# Revit family: ER
name_source: partatom
category: Wyposażenie mechaniczne
revit_build: Autodesk Revit 2017 (Build: 20160225_1515(x64)
units: mm (PartAtom-declared; Revit-internal decimal feet)

## family parameters
Oparty na płaszczyźnie roboczej = Nie
Punkt obliczania pomieszczeń = Nie
Tnij formami wycięć po wczytaniu = Nie
Typ części = Normalny
Współdzielony = Nie
Wymiar okrągłego złącza = Użyj średnicy
Zawsze pionowo = Tak

## types (28) — shared parameters
Date = 01.2019
Electrical_motor_diameter = 30 mm  [stored 0.0984252 ft]
Electrical_motor_length_front = 5 mm  [stored 0.0164042 ft]
Frequency = 50 Hz
Producent = Rosenberg
URL = https://www.rosenberg.pl
Version = 1
Voltage = 230 V

## per-type parameters (varying)
- 400-4.4EC: 250_cover=Nie; 315_cover=Nie; 400_cover=Tak; 450_cover=Nie; 560_cover=Nie; 630_cover=Nie; Air_flow=3245.0 m³/h; Current=1 A; Electrical_motor_length_back=60 mm  [stored 0.19685 ft]; Inner_diameter=403 mm; Length=155 mm  [stored 0.50853 ft]; Model=400-4.4EC; Outer_diameter=466 mm; Power=0 kW; Pressure=67.0 Pa; Propeller_length=197 mm  [stored 0.646325 ft]; Protection_class=IP54; Radius_inner=202 mm; Radius_outer=233 mm; Sheet_metal_thickness=6 mm  [stored 0.019685 ft]; Thickness=88 mm  [stored 0.288714 ft]; Weight=7.50 kg; Wymiar_obudowy/2=270 mm; diameter=409 mm; max.Ambient_temperature=60 °C
- 315-2: 250_cover=Nie; 315_cover=Tak; 400_cover=Nie; 450_cover=Nie; 560_cover=Nie; 630_cover=Nie; Air_flow=2796.0 m³/h; Current=3 A; Electrical_motor_length_back=85 mm  [stored 0.278871 ft]; Inner_diameter=317 mm; Length=130 mm  [stored 0.426509 ft]; Model=315-2; Outer_diameter=382 mm; Power=1 kW; Pressure=20.0 Pa; Propeller_length=154 mm; Protection_class=IP54; Radius_inner=159 mm; Radius_outer=191 mm  [stored 0.62664 ft]; Sheet_metal_thickness=6 mm  [stored 0.019685 ft]; Thickness=49 mm  [stored 0.160761 ft]; Weight=10.40 kg; Wymiar_obudowy/2=185 mm  [stored 0.606955 ft]; diameter=323 mm; max.Ambient_temperature=50 °C
- 250-2.3CF: 250_cover=Tak; 315_cover=Nie; 400_cover=Nie; 450_cover=Nie; 560_cover=Nie; 630_cover=Nie; Air_flow=0.0 m³/h; Current=1 A; Electrical_motor_length_back=61 mm  [stored 0.200131 ft]; Inner_diameter=254 mm; Length=95 mm  [stored 0.31168 ft]; Model=250-2.3CF; Outer_diameter=306 mm; Power=0 kW; Pressure=0.0 Pa; Propeller_length=122 mm; Protection_class=IP44; Radius_inner=127 mm  [stored 0.416667 ft]; Radius_outer=153 mm  [stored 0.501969 ft]; Sheet_metal_thickness=6 mm  [stored 0.019685 ft]; Thickness=46 mm  [stored 0.150919 ft]; Weight=3.50 kg; Wymiar_obudowy/2=156 mm  [stored 0.511811 ft]; diameter=260 mm; max.Ambient_temperature=60 °C
- 350-2: 250_cover=Nie; 315_cover=Nie; 400_cover=Tak; 450_cover=Nie; 560_cover=Nie; 630_cover=Nie; Air_flow=3738.0 m³/h; Current=4 A; Electrical_motor_length_back=60 mm  [stored 0.19685 ft]; Inner_diameter=358 mm; Length=135 mm  [stored 0.442913 ft]; Model=350-2; Outer_diameter=421 mm; Power=1 kW; Pressure=217.0 Pa; Propeller_length=174 mm  [stored 0.570866 ft]; Protection_class=IP54; Radius_inner=179 mm  [stored 0.58727 ft]; Radius_outer=211 mm; Sheet_metal_thickness=12 mm  [stored 0.0393701 ft]; Thickness=74 mm  [stored 0.242782 ft]; Weight=12.50 kg; Wymiar_obudowy/2=243 mm; diameter=364 mm; max.Ambient_temperature=40 °C
- 500-6: 250_cover=Nie; 315_cover=Nie; 400_cover=Nie; 450_cover=Tak; 560_cover=Nie; 630_cover=Nie; Air_flow=3652.0 m³/h; Current=1 A; Electrical_motor_length_back=60 mm  [stored 0.19685 ft]; Inner_diameter=504 mm; Length=165 mm; Model=500-6; Outer_diameter=567 mm; Power=0 kW; Pressure=49.0 Pa; Propeller_length=247 mm; Protection_class=IP54; Radius_inner=252 mm; Radius_outer=284 mm; Sheet_metal_thickness=12 mm  [stored 0.0393701 ft]; Thickness=88 mm  [stored 0.288714 ft]; Weight=10.50 kg; Wymiar_obudowy/2=270 mm; diameter=510 mm; max.Ambient_temperature=60 °C
- 560-4: 250_cover=Nie; 315_cover=Nie; 400_cover=Nie; 450_cover=Nie; 560_cover=Tak; 630_cover=Nie; Air_flow=7173.0 m³/h; Current=4 A; Electrical_motor_length_back=60 mm  [stored 0.19685 ft]; Inner_diameter=561 mm; Length=210 mm  [stored 0.688976 ft]; Model=560-4; Outer_diameter=630 mm; Power=1 kW; Pressure=124.0 Pa; Propeller_length=275 mm; Protection_class=IP54; Radius_inner=280 mm; Radius_outer=315 mm; Sheet_metal_thickness=12 mm  [stored 0.0393701 ft]; Thickness=88 mm  [stored 0.288714 ft]; Weight=16.50 kg; Wymiar_obudowy/2=270 mm; diameter=567 mm; max.Ambient_temperature=40 °C
- 630-4: 250_cover=Nie; 315_cover=Nie; 400_cover=Nie; 450_cover=Nie; 560_cover=Nie; 630_cover=Tak; Air_flow=12288.0 m³/h; Current=10 A; Electrical_motor_length_back=60 mm  [stored 0.19685 ft]; Inner_diameter=635 mm; Length=220 mm  [stored 0.721785 ft]; Model=630-4; Outer_diameter=704 mm; Power=2 kW; Pressure=204.0 Pa; Propeller_length=313 mm; Protection_class=IP54; Radius_inner=318 mm; Radius_outer=352 mm; Sheet_metal_thickness=12 mm  [stored 0.0393701 ft]; Thickness=88 mm  [stored 0.288714 ft]; Weight=22.50 kg; Wymiar_obudowy/2=270 mm; diameter=641 mm; max.Ambient_temperature=40 °C
- 315-2.4FF: 250_cover=Nie; 315_cover=Tak; 400_cover=Nie; 450_cover=Nie; 560_cover=Nie; 630_cover=Nie; Air_flow=2499.0 m³/h; Current=2 A; Electrical_motor_length_back=85 mm  [stored 0.278871 ft]; Inner_diameter=317 mm; Length=130 mm  [stored 0.426509 ft]; Model=315-2.4FF; Outer_diameter=382 mm; Power=0 kW; Pressure=168.0 Pa; Propeller_length=154 mm; Protection_class=IP54; Radius_inner=159 mm; Radius_outer=191 mm  [stored 0.62664 ft]; Sheet_metal_thickness=6 mm  [stored 0.019685 ft]; Thickness=49 mm  [stored 0.160761 ft]; Weight=6.20 kg; Wymiar_obudowy/2=185 mm  [stored 0.606955 ft]; diameter=323 mm; max.Ambient_temperature=50 °C
- 315-4.4DA: 250_cover=Nie; 315_cover=Tak; 400_cover=Nie; 450_cover=Nie; 560_cover=Nie; 630_cover=Nie; Air_flow=0.0 m³/h; Current=1 A; Electrical_motor_length_back=85 mm  [stored 0.278871 ft]; Inner_diameter=317 mm; Length=130 mm  [stored 0.426509 ft]; Model=315-4.4DA; Outer_diameter=382 mm; Power=0 kW; Pressure=0.0 Pa; Propeller_length=154 mm; Protection_class=IP54; Radius_inner=159 mm; Radius_outer=191 mm  [stored 0.62664 ft]; Sheet_metal_thickness=6 mm  [stored 0.019685 ft]; Thickness=49 mm  [stored 0.160761 ft]; Weight=6.00 kg; Wymiar_obudowy/2=185 mm  [stored 0.606955 ft]; diameter=323 mm; max.Ambient_temperature=65 °C
- 350-4: 250_cover=Nie; 315_cover=Nie; 400_cover=Tak; 450_cover=Nie; 560_cover=Nie; 630_cover=Nie; Air_flow=2255.0 m³/h; Current=1 A; Electrical_motor_length_back=60 mm  [stored 0.19685 ft]; Inner_diameter=358 mm; Length=135 mm  [stored 0.442913 ft]; Model=350-4; Outer_diameter=421 mm; Power=0 kW; Pressure=57.0 Pa; Propeller_length=174 mm  [stored 0.570866 ft]; Protection_class=IP54; Radius_inner=179 mm  [stored 0.58727 ft]; Radius_outer=211 mm; Sheet_metal_thickness=12 mm  [stored 0.0393701 ft]; Thickness=74 mm  [stored 0.242782 ft]; Weight=10.00 kg; Wymiar_obudowy/2=243 mm; diameter=364 mm; max.Ambient_temperature=65 °C
- 350-4.4EC: 250_cover=Nie; 315_cover=Nie; 400_cover=Tak; 450_cover=Nie; 560_cover=Nie; 630_cover=Nie; Air_flow=2150.0 m³/h; Current=1 A; Electrical_motor_length_back=60 mm  [stored 0.19685 ft]; Inner_diameter=358 mm; Length=135 mm  [stored 0.442913 ft]; Model=350-4.4EC; Outer_diameter=421 mm; Power=0 kW; Pressure=78.0 Pa; Propeller_length=174 mm  [stored 0.570866 ft]; Protection_class=IP54; Radius_inner=179 mm  [stored 0.58727 ft]; Radius_outer=211 mm; Sheet_metal_thickness=12 mm  [stored 0.0393701 ft]; Thickness=74 mm  [stored 0.242782 ft]; Weight=7.00 kg; Wymiar_obudowy/2=243 mm; diameter=364 mm; max.Ambient_temperature=70 °C
- 400-6.4DA: 250_cover=Nie; 315_cover=Nie; 400_cover=Tak; 450_cover=Nie; 560_cover=Nie; 630_cover=Nie; Air_flow=0.0 m³/h; Current=0 A; Electrical_motor_length_back=60 mm  [stored 0.19685 ft]; Inner_diameter=403 mm; Length=155 mm  [stored 0.50853 ft]; Model=400-6.DA; Outer_diameter=466 mm; Power=0 kW; Pressure=0.0 Pa; Propeller_length=197 mm  [stored 0.646325 ft]; Protection_class=IP54; Radius_inner=202 mm; Radius_outer=233 mm; Sheet_metal_thickness=6 mm  [stored 0.019685 ft]; Thickness=88 mm  [stored 0.288714 ft]; Weight=8.50 kg; Wymiar_obudowy/2=270 mm; diameter=409 mm; max.Ambient_temperature=55 °C
- 450-4.5DF: 250_cover=Nie; 315_cover=Nie; 400_cover=Nie; 450_cover=Tak; 560_cover=Nie; 630_cover=Nie; Air_flow=4055.0 m³/h; Current=1 A; Electrical_motor_length_back=60 mm  [stored 0.19685 ft]; Inner_diameter=452 mm; Length=160 mm  [stored 0.524934 ft]; Model=450-4.5DF; Outer_diameter=515 mm; Power=0 kW; Pressure=92.0 Pa; Propeller_length=221 mm; Protection_class=IP54; Radius_inner=226 mm  [stored 0.74147 ft]; Radius_outer=258 mm; Sheet_metal_thickness=6 mm  [stored 0.019685 ft]; Thickness=88 mm  [stored 0.288714 ft]; Weight=10.00 kg; Wymiar_obudowy/2=270 mm; diameter=458 mm; max.Ambient_temperature=5 °C
- 450-6.5DF: 250_cover=Nie; 315_cover=Nie; 400_cover=Nie; 450_cover=Tak; 560_cover=Nie; 630_cover=Nie; Air_flow=0.0 m³/h; Current=1 A; Electrical_motor_length_back=60 mm  [stored 0.19685 ft]; Inner_diameter=452 mm; Length=160 mm  [stored 0.524934 ft]; Model=450-6.5DF; Outer_diameter=515 mm; Power=0 kW; Pressure=0.0 Pa; Propeller_length=221 mm; Protection_class=IP54; Radius_inner=226 mm  [stored 0.74147 ft]; Radius_outer=258 mm; Sheet_metal_thickness=6 mm  [stored 0.019685 ft]; Thickness=88 mm  [stored 0.288714 ft]; Weight=9.00 kg; Wymiar_obudowy/2=270 mm; diameter=458 mm; max.Ambient_temperature=70 °C
- 500-4.5FA: 250_cover=Nie; 315_cover=Nie; 400_cover=Nie; 450_cover=Tak; 560_cover=Nie; 630_cover=Nie; Air_flow=5483.0 m³/h; Current=2 A; Electrical_motor_length_back=60 mm  [stored 0.19685 ft]; Inner_diameter=504 mm; Length=165 mm; Model=500-4.5FA; Outer_diameter=567 mm; Power=0 kW; Pressure=108.0 Pa; Propeller_length=247 mm; Protection_class=IP54; Radius_inner=252 mm; Radius_outer=284 mm; Sheet_metal_thickness=12 mm  [stored 0.0393701 ft]; Thickness=88 mm  [stored 0.288714 ft]; Weight=12.00 kg; Wymiar_obudowy/2=270 mm; diameter=510 mm; max.Ambient_temperature=50 °C
- 560-6.5FA: 250_cover=Nie; 315_cover=Nie; 400_cover=Nie; 450_cover=Nie; 560_cover=Tak; 630_cover=Nie; Air_flow=5680.0 m³/h; Current=2 A; Electrical_motor_length_back=60 mm  [stored 0.19685 ft]; Inner_diameter=561 mm; Length=210 mm  [stored 0.688976 ft]; Model=560-6.5FA; Outer_diameter=630 mm; Power=0 kW; Pressure=65.0 Pa; Propeller_length=275 mm; Protection_class=IP54; Radius_inner=280 mm; Radius_outer=315 mm; Sheet_metal_thickness=12 mm  [stored 0.0393701 ft]; Thickness=88 mm  [stored 0.288714 ft]; Weight=14.00 kg; Wymiar_obudowy/2=270 mm; diameter=567 mm; max.Ambient_temperature=60 °C
- 630-6.5HA: 250_cover=Nie; 315_cover=Nie; 400_cover=Nie; 450_cover=Nie; 560_cover=Nie; 630_cover=Tak; Air_flow=7647.0 m³/h; Current=2 A; Electrical_motor_length_back=60 mm  [stored 0.19685 ft]; Inner_diameter=635 mm; Length=220 mm  [stored 0.721785 ft]; Model=630-6.5HA; Outer_diameter=704 mm; Power=0 kW; Pressure=70.0 Pa; Propeller_length=313 mm; Protection_class=IP54; Radius_inner=318 mm; Radius_outer=352 mm; Sheet_metal_thickness=12 mm  [stored 0.0393701 ft]; Thickness=88 mm  [stored 0.288714 ft]; Weight=22.50 kg; Wymiar_obudowy/2=270 mm; diameter=641 mm; max.Ambient_temperature=60 °C
- 710-6: 250_cover=Nie; 315_cover=Nie; 400_cover=Nie; 450_cover=Nie; 560_cover=Nie; 630_cover=Nie; Air_flow=10559.0 m³/h; Current=5 A; Electrical_motor_length_back=60 mm  [stored 0.19685 ft]; Inner_diameter=711 mm; Length=230 mm  [stored 0.754593 ft]; Model=710-6; Outer_diameter=785 mm; Power=1 kW; Pressure=91.0 Pa; Propeller_length=351 mm; Protection_class=IP54; Radius_inner=356 mm; Radius_outer=393 mm; Sheet_metal_thickness=12 mm  [stored 0.0393701 ft]; Thickness=88 mm  [stored 0.288714 ft]; Weight=31.00 kg; Wymiar_obudowy/2=270 mm; diameter=717 mm; max.Ambient_temperature=70 °C
- 200-2.3BF: 250_cover=Tak; 315_cover=Nie; 400_cover=Nie; 450_cover=Nie; 560_cover=Nie; 630_cover=Nie; Air_flow=0.0 m³/h; Current=0 A; Electrical_motor_length_back=61 mm  [stored 0.200131 ft]; Inner_diameter=204 mm; Length=93 mm  [stored 0.305118 ft]; Model=200-2.3BF; Outer_diameter=255 mm; Power=0 kW; Pressure=0.0 Pa; Propeller_length=97 mm; Protection_class=IP44; Radius_inner=102 mm; Radius_outer=128 mm; Sheet_metal_thickness=6 mm  [stored 0.019685 ft]; Thickness=46 mm  [stored 0.150919 ft]; Weight=2.50 kg; Wymiar_obudowy/2=156 mm  [stored 0.511811 ft]; diameter=210 mm  [stored 0.688976 ft]; max.Ambient_temperature=70 °C
- 200-4.3BF: 250_cover=Tak; 315_cover=Nie; 400_cover=Nie; 450_cover=Nie; 560_cover=Nie; 630_cover=Nie; Air_flow=0.0 m³/h; Current=0 A; Electrical_motor_length_back=61 mm  [stored 0.200131 ft]; Inner_diameter=204 mm; Length=93 mm  [stored 0.305118 ft]; Model=200-4.3BF; Outer_diameter=255 mm; Power=0 kW; Pressure=0.0 Pa; Propeller_length=97 mm; Protection_class=IP44; Radius_inner=102 mm; Radius_outer=128 mm; Sheet_metal_thickness=6 mm  [stored 0.019685 ft]; Thickness=46 mm  [stored 0.150919 ft]; Weight=2.50 kg; Wymiar_obudowy/2=156 mm  [stored 0.511811 ft]; diameter=210 mm  [stored 0.688976 ft]; max.Ambient_temperature=70 °C
- 250-4.3CF: 250_cover=Tak; 315_cover=Nie; 400_cover=Nie; 450_cover=Nie; 560_cover=Nie; 630_cover=Nie; Air_flow=0.0 m³/h; Current=0 A; Electrical_motor_length_back=61 mm  [stored 0.200131 ft]; Inner_diameter=254 mm; Length=95 mm  [stored 0.31168 ft]; Model=250-4.3CF; Outer_diameter=306 mm; Power=0 kW; Pressure=0.0 Pa; Propeller_length=122 mm; Protection_class=IP44; Radius_inner=127 mm  [stored 0.416667 ft]; Radius_outer=153 mm  [stored 0.501969 ft]; Sheet_metal_thickness=6 mm  [stored 0.019685 ft]; Thickness=46 mm  [stored 0.150919 ft]; Weight=3.50 kg; Wymiar_obudowy/2=156 mm  [stored 0.511811 ft]; diameter=260 mm; max.Ambient_temperature=70 °C
- 300-2.3EF: 250_cover=Nie; 315_cover=Tak; 400_cover=Nie; 450_cover=Nie; 560_cover=Nie; 630_cover=Nie; Air_flow=1848.0 m³/h; Current=1 A; Electrical_motor_length_back=85 mm  [stored 0.278871 ft]; Inner_diameter=317 mm; Length=130 mm  [stored 0.426509 ft]; Model=300-2.3EF; Outer_diameter=382 mm; Power=0 kW; Pressure=126.0 Pa; Propeller_length=154 mm; Protection_class=IP44; Radius_inner=159 mm; Radius_outer=191 mm  [stored 0.62664 ft]; Sheet_metal_thickness=6 mm  [stored 0.019685 ft]; Thickness=49 mm  [stored 0.160761 ft]; Weight=5.50 kg; Wymiar_obudowy/2=185 mm  [stored 0.606955 ft]; diameter=323 mm; max.Ambient_temperature=55 °C
- 300-4.3DF: 250_cover=Nie; 315_cover=Tak; 400_cover=Nie; 450_cover=Nie; 560_cover=Nie; 630_cover=Nie; Air_flow=0.0 m³/h; Current=0 A; Electrical_motor_length_back=85 mm  [stored 0.278871 ft]; Inner_diameter=317 mm; Length=130 mm  [stored 0.426509 ft]; Model=300-4.3DF; Outer_diameter=382 mm; Power=0 kW; Pressure=0.0 Pa; Propeller_length=154 mm; Protection_class=IP44; Radius_inner=159 mm; Radius_outer=191 mm  [stored 0.62664 ft]; Sheet_metal_thickness=6 mm  [stored 0.019685 ft]; Thickness=49 mm  [stored 0.160761 ft]; Weight=5.50 kg; Wymiar_obudowy/2=185 mm  [stored 0.606955 ft]; diameter=323 mm; max.Ambient_temperature=55 °C
- 315-6.4DA: 250_cover=Nie; 315_cover=Tak; 400_cover=Nie; 450_cover=Nie; 560_cover=Nie; 630_cover=Nie; Air_flow=0.0 m³/h; Current=0 A; Electrical_motor_length_back=85 mm  [stored 0.278871 ft]; Inner_diameter=317 mm; Length=130 mm  [stored 0.426509 ft]; Model=315-6.4DA; Outer_diameter=382 mm; Power=0 kW; Pressure=0.0 Pa; Propeller_length=154 mm; Protection_class=IP54; Radius_inner=159 mm; Radius_outer=191 mm  [stored 0.62664 ft]; Sheet_metal_thickness=6 mm  [stored 0.019685 ft]; Thickness=49 mm  [stored 0.160761 ft]; Weight=6.50 kg; Wymiar_obudowy/2=185 mm  [stored 0.606955 ft]; diameter=323 mm; max.Ambient_temperature=60 °C
- 350-6.4DA: 250_cover=Nie; 315_cover=Nie; 400_cover=Tak; 450_cover=Nie; 560_cover=Nie; 630_cover=Nie; Air_flow=0.0 m³/h; Current=0 A; Electrical_motor_length_back=60 mm  [stored 0.19685 ft]; Inner_diameter=358 mm; Length=135 mm  [stored 0.442913 ft]; Model=350-6.4DA; Outer_diameter=421 mm; Power=0 kW; Pressure=0.0 Pa; Propeller_length=174 mm  [stored 0.570866 ft]; Protection_class=IP54; Radius_inner=179 mm  [stored 0.58727 ft]; Radius_outer=211 mm; Sheet_metal_thickness=12 mm  [stored 0.0393701 ft]; Thickness=74 mm  [stored 0.242782 ft]; Weight=7.00 kg; Wymiar_obudowy/2=243 mm; diameter=364 mm; max.Ambient_temperature=60 °C
- 560-4 (6HF): 250_cover=Nie; 315_cover=Nie; 400_cover=Nie; 450_cover=Nie; 560_cover=Tak; 630_cover=Nie; Air_flow=8171.0 m³/h; Current=6 A; Electrical_motor_length_back=60 mm  [stored 0.19685 ft]; Inner_diameter=561 mm; Length=210 mm  [stored 0.688976 ft]; Model=560-4 (6HF); Outer_diameter=630 mm; Power=1 kW; Pressure=150.0 Pa; Propeller_length=275 mm; Protection_class=IP54; Radius_inner=280 mm; Radius_outer=315 mm; Sheet_metal_thickness=12 mm  [stored 0.0393701 ft]; Thickness=88 mm  [stored 0.288714 ft]; Weight=0.00 kg; Wymiar_obudowy/2=270 mm; diameter=567 mm; max.Ambient_temperature=60 °C
- 560-4.5HA: 250_cover=Nie; 315_cover=Nie; 400_cover=Nie; 450_cover=Nie; 560_cover=Tak; 630_cover=Nie; Air_flow=8442.0 m³/h; Current=4 A; Electrical_motor_length_back=60 mm  [stored 0.19685 ft]; Inner_diameter=561 mm; Length=210 mm  [stored 0.688976 ft]; Model=560-4.5HA; Outer_diameter=630 mm; Power=1 kW; Pressure=134.0 Pa; Propeller_length=275 mm; Protection_class=IP54; Radius_inner=280 mm; Radius_outer=315 mm; Sheet_metal_thickness=12 mm  [stored 0.0393701 ft]; Thickness=88 mm  [stored 0.288714 ft]; Weight=17.00 kg; Wymiar_obudowy/2=270 mm; diameter=567 mm; max.Ambient_temperature=40 °C
- 560-6.5KA: 250_cover=Nie; 315_cover=Nie; 400_cover=Nie; 450_cover=Nie; 560_cover=Tak; 630_cover=Nie; Air_flow=5327.0 m³/h; Current=2 A; Electrical_motor_length_back=60 mm  [stored 0.19685 ft]; Inner_diameter=561 mm; Length=210 mm  [stored 0.688976 ft]; Model=560-6.5KA; Outer_diameter=630 mm; Power=1 kW; Pressure=106.0 Pa; Propeller_length=275 mm; Protection_class=IP54; Radius_inner=280 mm; Radius_outer=315 mm; Sheet_metal_thickness=12 mm  [stored 0.0393701 ft]; Thickness=88 mm  [stored 0.288714 ft]; Weight=19.00 kg; Wymiar_obudowy/2=270 mm; diameter=567 mm; max.Ambient_temperature=65 °C

note: [stored X ft] marks values corroborated as IEEE doubles in the binary element streams (Revit-internal decimal feet)
